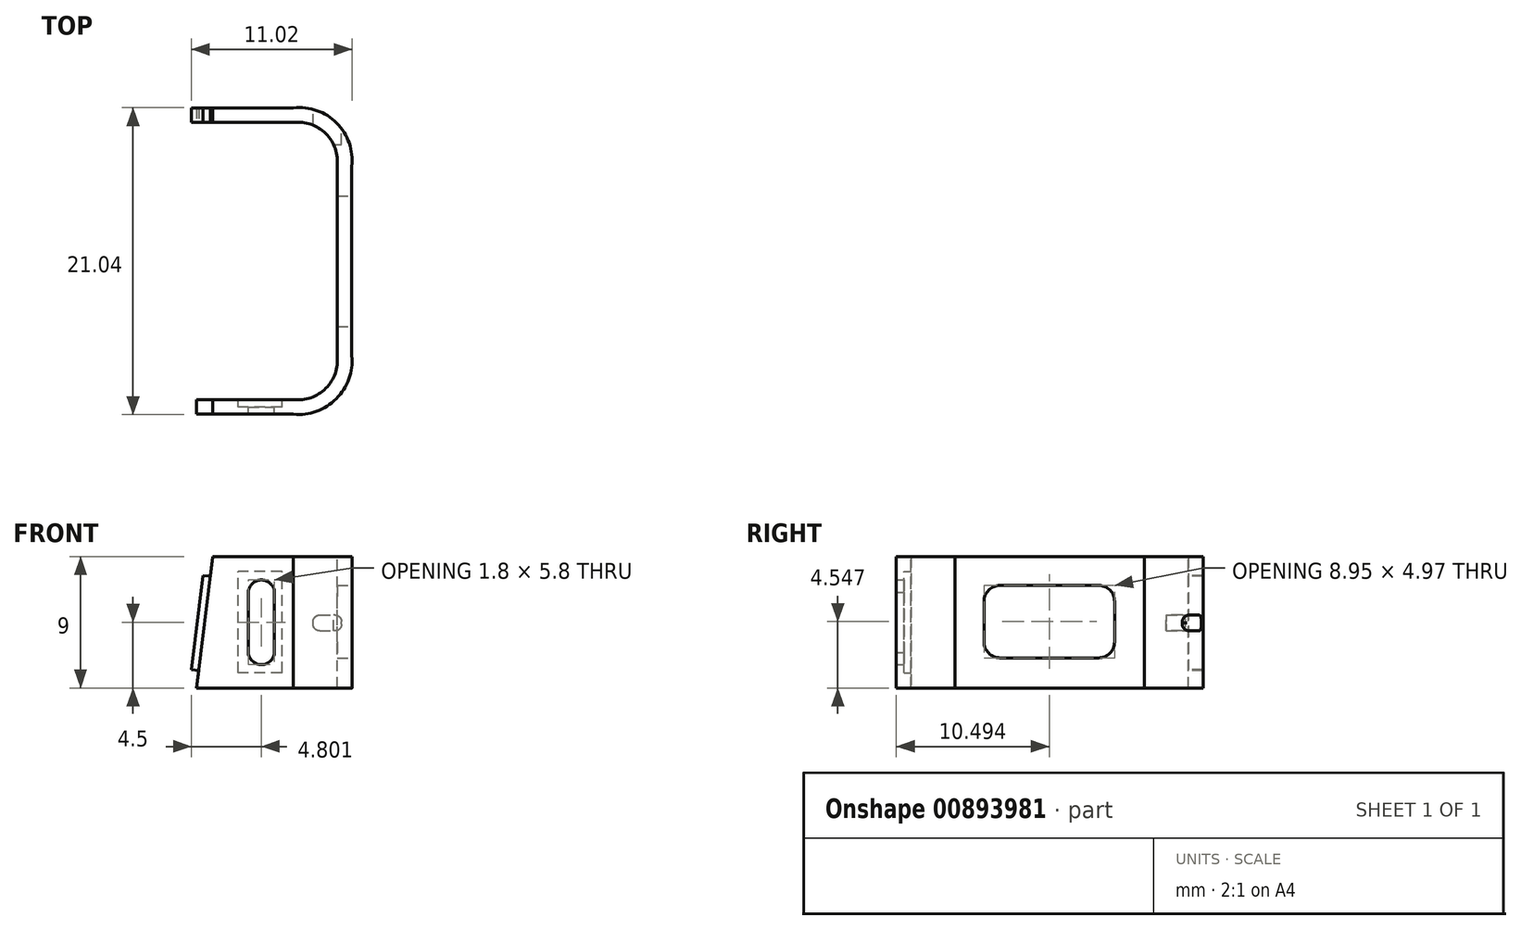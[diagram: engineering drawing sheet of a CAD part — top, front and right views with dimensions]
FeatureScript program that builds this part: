
annotation { "Feature Type Name" : "Feature", "Feature Type Description" : "" }
export const myFeature = defineFeature(function(context is Context, id is Id, definition is map)
    precondition{}
    {
        {
            var Q0;
            Q0=qCreatedBy(makeId("Top.planeOp"),FACE);
            var sketch = newSketch(context, id + "F0", { "sketchPlane" : qUnion([Q0])});
            skLineSegment(sketch, "E0", {"start": v(-1.08, -14.75) * mm, "end": v(-7.73, -14.75) * mm});
            skLineSegment(sketch, "E1", {"start": v(-1.08, 6.25) * mm, "end": v(-8.08, 6.25) * mm});
            skLineSegment(sketch, "E2", {"start": v(-8.08, 6.25) * mm, "end": v(-8.08, 5.25) * mm});
            skLineSegment(sketch, "E3", {"start": v(-8.08, 5.25) * mm, "end": v(-1.08, 5.25) * mm});
            skArc(sketch, "E4", {"start": v(1.92, 2.25) * mm, "mid": v(1.15, 4.48) * mm, "end": v(-1.08, 5.25) * mm});
            skLineSegment(sketch, "E5", {"start": v(1.92, 2.25) * mm, "end": v(1.92, -10.75) * mm});
            skArc(sketch, "E6", {"start": v(-1.08, -13.75) * mm, "mid": v(1.14, -12.97) * mm, "end": v(1.92, -10.75) * mm});
            skArc(sketch, "E7", {"start": v(-1.08, -14.75) * mm, "mid": v(1.86, -13.7) * mm, "end": v(2.92, -10.75) * mm});
            skLineSegment(sketch, "E8", {"start": v(2.92, -10.75) * mm, "end": v(2.92, 2.25) * mm});
            skArc(sketch, "E9", {"start": v(2.92, 2.25) * mm, "mid": v(1.89, 5.22) * mm, "end": v(-1.08, 6.25) * mm});
            skLineSegment(sketch, "E10", {"start": v(-7.73, -14.75) * mm, "end": v(-7.73, -13.75) * mm});
            skLineSegment(sketch, "E11", {"start": v(-7.73, -13.75) * mm, "end": v(-1.08, -13.75) * mm});
            skSolve(sketch);
        }
        {
            var Q0;
            Q0 = qSketchRegion(id + "F0", true);
            extrude(context, id + "F1", {"entities" : qUnion([Q0]), "oppositeDirection" : true, "depth" : 4.5 * mm, "offsetDistance" : 25 * mm, "hasSecondDirection" : true, "secondDirectionOppositeDirection" : false, "secondDirectionDepth" : 4.5 * mm});
        }
        {
            var Q0;
            Q0=makeQuery(id+"F1.opExtrude","SWEPT_FACE",FACE,{"disambiguationData":[OSD([sQuery(id+"F0.wireOp",EDGE,"E8")])]});
            var sketch = newSketch(context, id + "F2", { "sketchPlane" : qUnion([Q0])});
            skLineSegment(sketch, "E12.bottom", {"start": v(-7.66, 2.53) * mm, "end": v(-0.9, 2.53) * mm});
            skLineSegment(sketch, "E12.top", {"start": v(-7.66, -2.44) * mm, "end": v(-0.9, -2.44) * mm});
            skLineSegment(sketch, "E12.left", {"start": v(-8.75, 1.44) * mm, "end": v(-8.75, -1.34) * mm});
            skLineSegment(sketch, "E12.right", {"start": v(0.2, 1.44) * mm, "end": v(0.2, -1.34) * mm});
            skPoint(sketch, "E13.visualSharp", {"position": v(-8.75, 2.53) * mm});
            skArc(sketch, "E13.filletArc", {"start": v(-7.66, 2.53) * mm, "mid": v(-8.43, 2.2) * mm, "end": v(-8.75, 1.44) * mm});
            skPoint(sketch, "E14.visualSharp", {"position": v(0.2, 2.53) * mm});
            skArc(sketch, "E14.filletArc", {"start": v(0.2, 1.44) * mm, "mid": v(-0.12, 2.2) * mm, "end": v(-0.9, 2.53) * mm});
            skPoint(sketch, "E15.visualSharp", {"position": v(0.2, -2.44) * mm});
            skArc(sketch, "E15.filletArc", {"start": v(-0.9, -2.44) * mm, "mid": v(-0.12, -2.12) * mm, "end": v(0.2, -1.34) * mm});
            skPoint(sketch, "E16.visualSharp", {"position": v(-8.75, -2.44) * mm});
            skArc(sketch, "E16.filletArc", {"start": v(-8.75, -1.34) * mm, "mid": v(-8.43, -2.12) * mm, "end": v(-7.66, -2.44) * mm});
            skSolve(sketch);
        }
        {
            var Q0;
            Q0=makeQuery(id+"F2.imprint","IMPRINT",FACE,{"disambiguationData":[TD([[makeQuery(id+"F2.imprint","IMPRINT",EDGE,{"derivedFrom":sQuery(id+"F2.wireOp",EDGE,"E12.bottom")}),-1.0]])]});
            extrude(context, id + "F3", {"entities" : qUnion([Q0]), "operationType" : NewBodyOperationType.REMOVE, "oppositeDirection" : true, "depth" : 2 * mm, "offsetDistance" : 25 * mm});
        }
        {
            var Q0;
            Q0=makeQuery(id+"F1.opExtrude","SWEPT_FACE",FACE,{"disambiguationData":[OSD([sQuery(id+"F0.wireOp",EDGE,"E1")])]});
            var sketch = newSketch(context, id + "F4", { "sketchPlane" : qUnion([Q0])});
            skLineSegment(sketch, "E17.bottom", {"start": v(-1.77, -0.59) * mm, "end": v(-0.7, -0.59) * mm});
            skLineSegment(sketch, "E17.top", {"start": v(-1.77, 0.5) * mm, "end": v(-0.7, 0.5) * mm});
            skLineSegment(sketch, "E17.left", {"start": v(-2.22, -0.15) * mm, "end": v(-2.22, 0.06) * mm});
            skLineSegment(sketch, "E17.right", {"start": v(-0.26, -0.15) * mm, "end": v(-0.26, 0.06) * mm});
            skPoint(sketch, "E18.visualSharp", {"position": v(-2.22, -0.59) * mm});
            skArc(sketch, "E18.filletArc", {"start": v(-2.22, -0.15) * mm, "mid": v(-2.09, -0.46) * mm, "end": v(-1.77, -0.59) * mm});
            skPoint(sketch, "E19.visualSharp", {"position": v(-2.22, 0.5) * mm});
            skArc(sketch, "E19.filletArc", {"start": v(-1.77, 0.5) * mm, "mid": v(-2.09, 0.37) * mm, "end": v(-2.22, 0.06) * mm});
            skPoint(sketch, "E20.visualSharp", {"position": v(-0.26, -0.59) * mm});
            skArc(sketch, "E20.filletArc", {"start": v(-0.7, -0.59) * mm, "mid": v(-0.4, -0.46) * mm, "end": v(-0.26, -0.15) * mm});
            skPoint(sketch, "E21.visualSharp", {"position": v(-0.26, 0.5) * mm});
            skArc(sketch, "E21.filletArc", {"start": v(-0.26, 0.06) * mm, "mid": v(-0.4, 0.37) * mm, "end": v(-0.7, 0.5) * mm});
            skSolve(sketch);
        }
        {
            var Q0;
            Q0=makeQuery(id+"F4.imprint","IMPRINT",FACE,{"disambiguationData":[TD([[makeQuery(id+"F4.imprint","IMPRINT",EDGE,{"derivedFrom":sQuery(id+"F4.wireOp",EDGE,"E17.bottom")}),1.0]])]});
            extrude(context, id + "F5", {"entities" : qUnion([Q0]), "operationType" : NewBodyOperationType.REMOVE, "oppositeDirection" : true, "depth" : 2.5 * mm, "offsetDistance" : 25 * mm});
        }
        {
            var Q0;
            Q0=makeQuery(id+"F1.opExtrude","SWEPT_FACE",FACE,{"disambiguationData":[OSD([sQuery(id+"F0.wireOp",EDGE,"E11")])]});
            var sketch = newSketch(context, id + "F6", { "sketchPlane" : qUnion([Q0])});
            skLineSegment(sketch, "E22.bottom", {"start": v(1.87, -3.47) * mm, "end": v(4.86, -3.47) * mm});
            skLineSegment(sketch, "E22.top", {"start": v(1.87, 3.5) * mm, "end": v(4.86, 3.5) * mm});
            skLineSegment(sketch, "E22.left", {"start": v(1.87, -3.47) * mm, "end": v(1.87, 3.5) * mm});
            skLineSegment(sketch, "E22.right", {"start": v(4.86, -3.47) * mm, "end": v(4.86, 3.5) * mm});
            skLineSegment(sketch, "E23", {"start": v(2.38, 2.07) * mm, "end": v(2.38, -2.07) * mm});
            skArc(sketch, "E24", {"start": v(2.38, -2.07) * mm, "mid": v(3.28, -2.9) * mm, "end": v(4.18, -2.07) * mm});
            skLineSegment(sketch, "E25", {"start": v(4.18, -2.07) * mm, "end": v(4.18, 2.07) * mm});
            skArc(sketch, "E26", {"start": v(4.18, 2.07) * mm, "mid": v(3.28, 2.9) * mm, "end": v(2.38, 2.07) * mm});
            skSolve(sketch);
        }
        {
            var Q0;
            Q0=makeQuery(id+"F6.imprint","IMPRINT",FACE,{"disambiguationData":[TD([[makeQuery(id+"F6.imprint","IMPRINT",EDGE,{"derivedFrom":sQuery(id+"F6.wireOp",EDGE,"E22.bottom")}),1.0]])]});
            extrude(context, id + "F7", {"entities" : qUnion([Q0]), "operationType" : NewBodyOperationType.REMOVE, "oppositeDirection" : true, "depth" : 0.5 * mm, "offsetDistance" : 25 * mm});
        }
        {
            var Q0;
            Q0=makeQuery(id+"F7.boolean.opBoolean","SPLIT",FACE,{"disambiguationData":[TD([makeQuery(id+"F7.opExtrude","SWEPT_FACE",FACE,{"disambiguationData":[OSD([sQuery(id+"F6.wireOp",EDGE,"E23")])]})])],"derivedFrom":makeQuery(id+"F1.opExtrude","SWEPT_FACE",FACE,{"disambiguationData":[OSD([sQuery(id+"F0.wireOp",EDGE,"E11")])]})});
            extrude(context, id + "F8", {"entities" : qUnion([Q0]), "operationType" : NewBodyOperationType.REMOVE, "oppositeDirection" : true, "depth" : 2 * mm, "offsetDistance" : 25 * mm});
        }
        {
            var Q0;
            Q0=makeQuery(id+"F1.opExtrude","SWEPT_FACE",FACE,{"disambiguationData":[OSD([sQuery(id+"F0.wireOp",EDGE,"E3")])]});
            var sketch = newSketch(context, id + "F9", { "sketchPlane" : qUnion([Q0])});
            skLineSegment(sketch, "E27", {"start": v(-1.46, -25.1) * mm, "end": v(-3.13, -15.97) * mm});
            skLineSegment(sketch, "E28", {"start": v(-3.13, -15.97) * mm, "end": v(-1006.7, -32.32) * mm});
            skLineSegment(sketch, "E29", {"start": v(-7.58, -3.3) * mm, "end": v(-8.08, -3.24) * mm});
            skLineSegment(sketch, "E30", {"start": v(-8.08, -3.24) * mm, "end": v(-8.08, -4.5) * mm});
            skLineSegment(sketch, "E31", {"start": v(-8.08, -4.5) * mm, "end": v(-7.73, -4.5) * mm});
            skLineSegment(sketch, "E32", {"start": v(-7.73, -4.5) * mm, "end": v(-7.58, -3.3) * mm});
            skLineSegment(sketch, "E33", {"start": v(-8.08, -3.24) * mm, "end": v(-8.08, 4.5) * mm});
            skLineSegment(sketch, "E34", {"start": v(-8.08, 4.5) * mm, "end": v(-6.62, 4.5) * mm});
            skLineSegment(sketch, "E35", {"start": v(-6.62, 4.5) * mm, "end": v(-6.8, 3.15) * mm});
            skLineSegment(sketch, "E36", {"start": v(-6.8, 3.15) * mm, "end": v(-7.29, 3.22) * mm});
            skLineSegment(sketch, "E37", {"start": v(-7.29, 3.22) * mm, "end": v(-8.08, -3.24) * mm});
            skSolve(sketch);
        }
        {
            var Q0;
            {var subQ0=sQuery(id+"F9.wireOp",EDGE,"E29");Q0=makeQuery(id+"F9.imprint","IMPRINT",FACE,{"disambiguationData":[TD([[makeQuery(id+"F9.imprint","IMPRINT",EDGE,{"derivedFrom":subQ0}),1.0]])]});}
            var Q1;
            {var subQ4=sQuery(id+"F9.wireOp",EDGE,"E33");Q1=makeQuery(id+"F9.imprint","IMPRINT",FACE,{"disambiguationData":[TD([[makeQuery(id+"F9.imprint","IMPRINT",EDGE,{"derivedFrom":subQ4}),-1.0]])]});}
            extrude(context, id + "F10", {"entities" : qUnion([Q0, Q1]), "operationType" : NewBodyOperationType.REMOVE, "oppositeDirection" : true, "depth" : 3 * mm, "offsetDistance" : 25 * mm});
        }
        {
            var Q0;
            {var subQ0=sQuery(id+"F0.wireOp",EDGE,"E6");var subQ2=sQuery(id+"F0.wireOp",EDGE,"E11");Q0=makeQuery(id+"F7.boolean.opBoolean","SPLIT",FACE,{"disambiguationData":[TD([makeQuery(id+"F1.opExtrude","SWEPT_FACE",FACE,{"disambiguationData":[OSD([subQ0])]})])],"derivedFrom":makeQuery(id+"F1.opExtrude","SWEPT_FACE",FACE,{"disambiguationData":[OSD([subQ2])]})});}
            var sketch = newSketch(context, id + "F11", { "sketchPlane" : qUnion([Q0])});
            skLineSegment(sketch, "E38", {"start": v(7.73, 4.5) * mm, "end": v(6.63, 4.5) * mm});
            skLineSegment(sketch, "E39", {"start": v(6.63, 4.5) * mm, "end": v(7.73, -4.5) * mm});
            skLineSegment(sketch, "E40", {"start": v(7.73, -4.5) * mm, "end": v(7.73, -4.5) * mm});
            skLineSegment(sketch, "E41", {"start": v(7.73, -4.5) * mm, "end": v(7.73, 4.5) * mm});
            skSolve(sketch);
        }
        {
            var Q0;
            {var subQ0=sQuery(id+"F11.wireOp",EDGE,"E40");Q0=makeQuery(id+"F11.imprint","IMPRINT",FACE,{"disambiguationData":[TD([[makeQuery(id+"F11.imprint","IMPRINT",EDGE,{"derivedFrom":subQ0}),-1.0]])]});}
            extrude(context, id + "F12", {"entities" : qUnion([Q0]), "operationType" : NewBodyOperationType.REMOVE, "oppositeDirection" : true, "depth" : 3 * mm, "offsetDistance" : 25 * mm});
        }
    });
